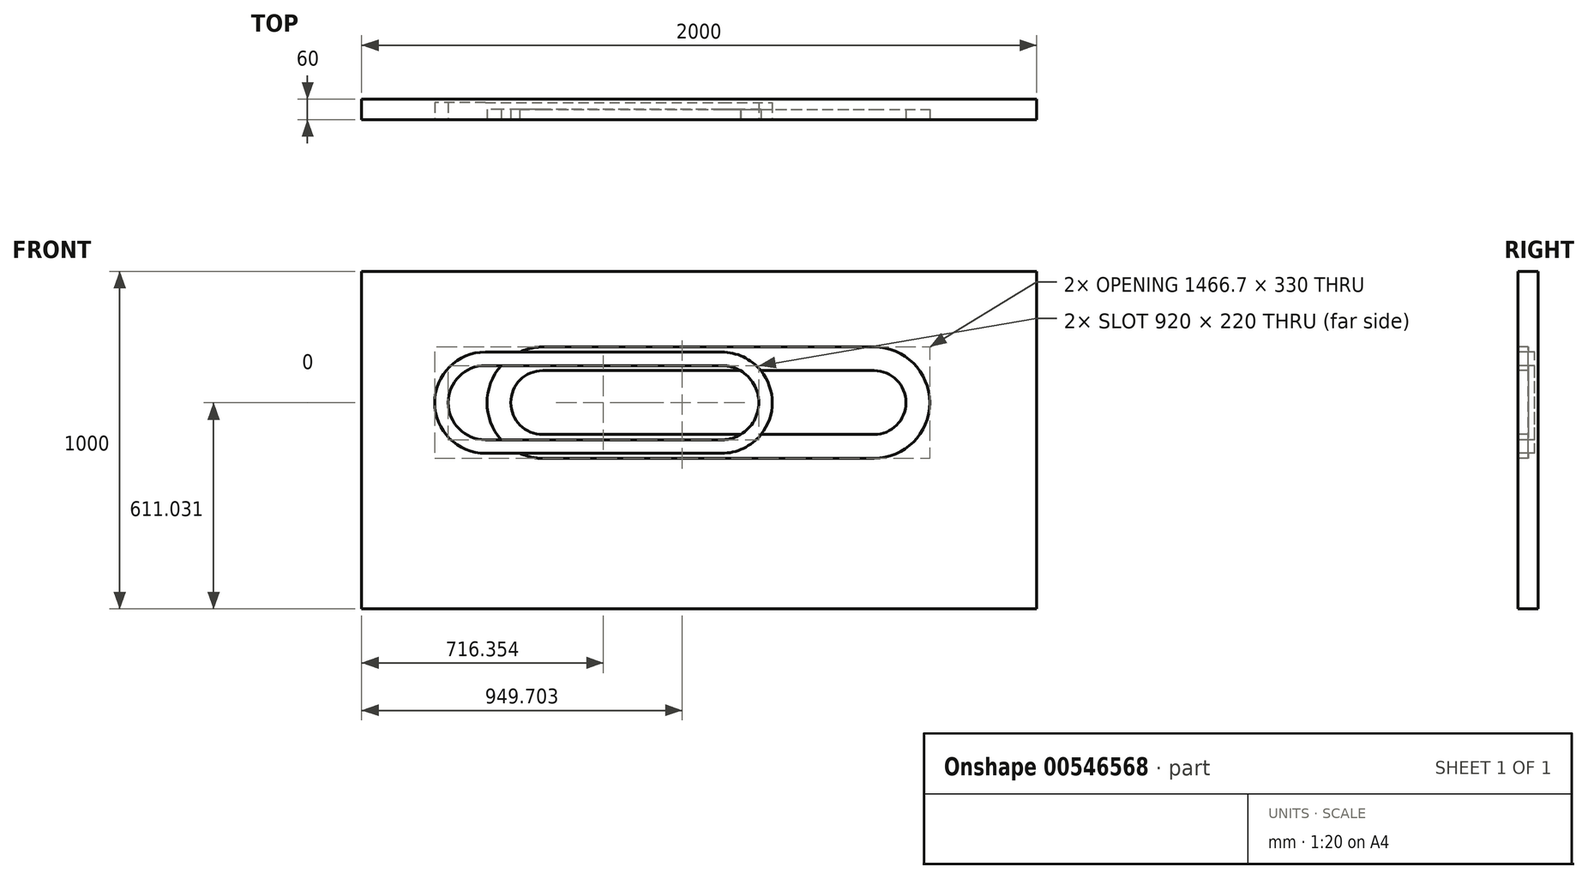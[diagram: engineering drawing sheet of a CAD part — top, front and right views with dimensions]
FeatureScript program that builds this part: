
annotation { "Feature Type Name" : "Feature", "Feature Type Description" : "" }
export const myFeature = defineFeature(function(context is Context, id is Id, definition is map)
    precondition{}
    {
        {
            var Q0;
            Q0=qCreatedBy(makeId("Front.planeOp"),FACE);
            var sketch = newSketch(context, id + "F0", { "sketchPlane" : qUnion([Q0])});
            skLineSegment(sketch, "E0.bottom", {"start": v(-999.78, 671.64) * mm, "end": v(1000.22, 671.64) * mm});
            skLineSegment(sketch, "E0.top", {"start": v(-999.78, -328.36) * mm, "end": v(1000.22, -328.36) * mm});
            skLineSegment(sketch, "E0.left", {"start": v(-999.78, 671.64) * mm, "end": v(-999.78, -328.36) * mm});
            skLineSegment(sketch, "E0.right", {"start": v(1000.22, 671.64) * mm, "end": v(1000.22, -328.36) * mm});
            skSolve(sketch);
        }
        {
            var Q0;
            Q0=makeQuery(id+"F0.imprint","IMPRINT",FACE,{"disambiguationData":[TD([[makeQuery(id+"F0.imprint","IMPRINT",EDGE,{"derivedFrom":sQuery(id+"F0.wireOp",EDGE,"E0.bottom")}),-1.0]])]});
            extrude(context, id + "F1", {"entities" : qUnion([Q0]), "depth" : 60 * mm, "offsetDistance" : 25 * mm});
        }
        {
            var Q0;
            Q0=makeQuery(id+"F1.opExtrude","CAP_FACE",FACE,{"disambiguationData":[OSD([sQuery(id+"F0.wireOp",EDGE,"E0.bottom"),sQuery(id+"F0.wireOp",EDGE,"E0.top"),sQuery(id+"F0.wireOp",EDGE,"E0.left"),sQuery(id+"F0.wireOp",EDGE,"E0.right")])],"isStart":false});
            var sketch = newSketch(context, id + "F2", { "sketchPlane" : qUnion([Q0])});
            skLineSegment(sketch, "E1", {"start": v(-633.43, 432.67) * mm, "end": v(66.57, 432.67) * mm});
            skLineSegment(sketch, "E2", {"start": v(-633.43, 132.67) * mm, "end": v(66.57, 132.67) * mm});
            skArc(sketch, "E3", {"start": v(-633.43, 432.67) * mm, "mid": v(-783.43, 282.67) * mm, "end": v(-633.43, 132.67) * mm});
            skLineSegment(sketch, "E4", {"start": v(-633.43, 392.67) * mm, "end": v(66.57, 392.67) * mm});
            skLineSegment(sketch, "E5", {"start": v(-633.43, 172.67) * mm, "end": v(66.57, 172.67) * mm});
            skArc(sketch, "E6", {"start": v(-633.43, 392.67) * mm, "mid": v(-743.43, 282.67) * mm, "end": v(-633.43, 172.67) * mm});
            skArc(sketch, "E7", {"start": v(66.57, 432.67) * mm, "mid": v(216.57, 282.67) * mm, "end": v(66.57, 132.67) * mm});
            skArc(sketch, "E8", {"start": v(66.57, 172.67) * mm, "mid": v(176.57, 282.67) * mm, "end": v(66.57, 392.67) * mm});
            skPoint(sketch, "E9.end.orphan", {"position": v(-591.38, 392.67) * mm});
            skPoint(sketch, "E9.start.orphan", {"position": v(-591.38, 432.67) * mm});
            skPoint(sketch, "E10.end.orphan", {"position": v(-589.06, 172.67) * mm});
            skPoint(sketch, "E10.start.orphan", {"position": v(-589.06, 132.67) * mm});
            skSolve(sketch);
        }
        {
            var Q0;
            Q0=makeQuery(id+"F2.imprint","IMPRINT",FACE,{"disambiguationData":[TD([[makeQuery(id+"F2.imprint","IMPRINT",EDGE,{"derivedFrom":sQuery(id+"F2.wireOp",EDGE,"E1")}),-1.0]])]});
            extrude(context, id + "F3", {"entities" : qUnion([Q0]), "operationType" : NewBodyOperationType.REMOVE, "oppositeDirection" : true, "depth" : 50 * mm, "offsetDistance" : 25 * mm});
        }
        {
            var Q0;
            {var subQ0=sQuery(id+"F0.wireOp",EDGE,"E0.left");var subQ1=sQuery(id+"F0.wireOp",EDGE,"E0.top");var subQ2=sQuery(id+"F0.wireOp",EDGE,"E0.right");var subQ3=sQuery(id+"F0.wireOp",EDGE,"E0.bottom");Q0=makeQuery(id+"F3.boolean.opBoolean","SPLIT",FACE,{"disambiguationData":[TD([makeQuery(id+"F1.opExtrude","SWEPT_FACE",FACE,{"disambiguationData":[OSD([subQ3])]})])],"derivedFrom":makeQuery(id+"F1.opExtrude","CAP_FACE",FACE,{"disambiguationData":[OSD([subQ3,subQ1,subQ0,subQ2])],"isStart":false})});}
            var sketch = newSketch(context, id + "F4", { "sketchPlane" : qUnion([Q0])});
            skLineSegment(sketch, "E11", {"start": v(-463.44, 447.67) * mm, "end": v(518.27, 447.67) * mm});
            skLineSegment(sketch, "E12", {"start": v(-463.44, 377.71) * mm, "end": v(518.27, 377.71) * mm});
            skLineSegment(sketch, "E13", {"start": v(-463.44, 188.27) * mm, "end": v(518.27, 188.27) * mm});
            skLineSegment(sketch, "E14", {"start": v(-463.44, 117.67) * mm, "end": v(518.27, 117.67) * mm});
            skPoint(sketch, "E15.end.orphan", {"position": v(-513.33, 447.67) * mm});
            skPoint(sketch, "E15.start.orphan", {"position": v(-513.33, 432.67) * mm});
            skPoint(sketch, "E16.end.orphan", {"position": v(-514.96, 377.71) * mm});
            skPoint(sketch, "E16.start.orphan", {"position": v(-514.96, 392.71) * mm});
            skPoint(sketch, "E17.end.orphan", {"position": v(-540.31, 188.27) * mm});
            skPoint(sketch, "E17.start.orphan", {"position": v(-540.31, 173.27) * mm});
            skPoint(sketch, "E18.end.orphan", {"position": v(-541.95, 117.67) * mm});
            skPoint(sketch, "E18.start.orphan", {"position": v(-541.95, 132.67) * mm});
            skArc(sketch, "E19", {"start": v(-463.44, 447.67) * mm, "mid": v(-628.44, 282.67) * mm, "end": v(-463.44, 117.67) * mm});
            skArc(sketch, "E20", {"start": v(-463.44, 377.71) * mm, "mid": v(-558.16, 283) * mm, "end": v(-463.44, 188.27) * mm});
            skArc(sketch, "E21", {"start": v(518.27, 377.71) * mm, "mid": v(613, 283) * mm, "end": v(518.27, 188.27) * mm});
            skArc(sketch, "E22", {"start": v(518.27, 447.67) * mm, "mid": v(683.27, 282.67) * mm, "end": v(518.27, 117.67) * mm});
            skSolve(sketch);
        }
        {
            var Q0;
            Q0 = qSketchRegion(id + "F4", true);
            extrude(context, id + "F5", {"entities" : qUnion([Q0]), "operationType" : NewBodyOperationType.REMOVE, "oppositeDirection" : true, "depth" : 30 * mm, "offsetDistance" : 25 * mm});
        }
    });
